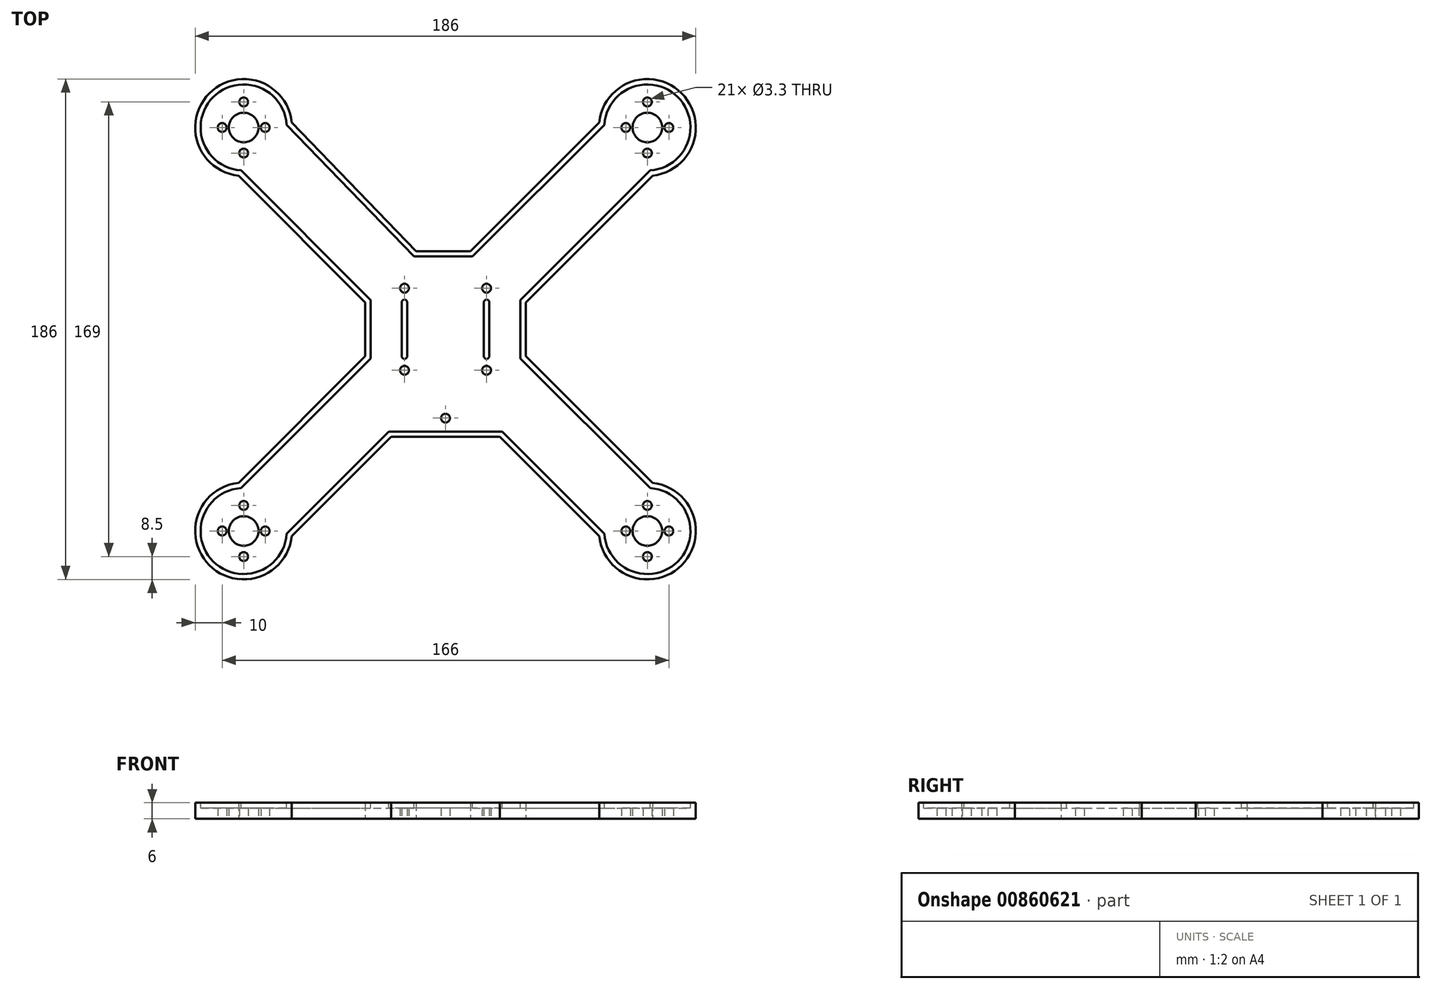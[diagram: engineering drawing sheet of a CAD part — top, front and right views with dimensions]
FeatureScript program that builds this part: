
annotation { "Feature Type Name" : "Feature", "Feature Type Description" : "" }
export const myFeature = defineFeature(function(context is Context, id is Id, definition is map)
    precondition{}
    {
        {
            var Q0;
            Q0=qCreatedBy(makeId("Top.planeOp"),FACE);
            var sketch = newSketch(context, id + "F0", { "sketchPlane" : qUnion([Q0])});
            skLineSegment(sketch, "E0.bottom", {"start": v(75, -75) * mm, "end": v(-75, -75) * mm, "construction": true});
            skLineSegment(sketch, "E0.top", {"start": v(75, 75) * mm, "end": v(-75, 75) * mm, "construction": true});
            skLineSegment(sketch, "E0.left", {"start": v(75, -75) * mm, "end": v(75, 75) * mm, "construction": true});
            skLineSegment(sketch, "E0.right", {"start": v(-75, -75) * mm, "end": v(-75, 75) * mm, "construction": true});
            skPoint(sketch, "E0.middle", {"position": v(0, 0) * mm});
            skLineSegment(sketch, "E1", {"start": v(-75, 75) * mm, "end": v(75, -75) * mm, "construction": true});
            skLineSegment(sketch, "E2", {"start": v(75, 75) * mm, "end": v(-75, -75) * mm, "construction": true});
            skCircle(sketch, "E3", {"center": v(-75, 75) * mm, "radius": 14 * mm, "construction": true});
            skCircle(sketch, "E4", {"center": v(75, 75) * mm, "radius": 14 * mm, "construction": true});
            skCircle(sketch, "E5", {"center": v(-75, -75) * mm, "radius": 14 * mm, "construction": true});
            skCircle(sketch, "E6", {"center": v(75, -75) * mm, "radius": 14 * mm, "construction": true});
            skCircle(sketch, "E7", {"center": v(-75, 75) * mm, "radius": 65 * mm, "construction": true});
            skCircle(sketch, "E8", {"center": v(75, 75) * mm, "radius": 65 * mm, "construction": true});
            skCircle(sketch, "E9", {"center": v(75, -75) * mm, "radius": 65 * mm, "construction": true});
            skCircle(sketch, "E10", {"center": v(-75, -75) * mm, "radius": 65 * mm, "construction": true});
            skPoint(sketch, "E11", {"position": v(29.04, 29.04) * mm});
            skPoint(sketch, "E12", {"position": v(-29.04, 29.04) * mm});
            skPoint(sketch, "E13", {"position": v(-29.04, -29.04) * mm});
            skPoint(sketch, "E14", {"position": v(29.04, -29.04) * mm});
            skLineSegment(sketch, "E15", {"start": v(-65.1, 84.9) * mm, "end": v(84.9, -65.1) * mm, "construction": true});
            skLineSegment(sketch, "E16", {"start": v(-84.9, 65.1) * mm, "end": v(65.1, -84.9) * mm, "construction": true});
            skLineSegment(sketch, "E17", {"start": v(-84.9, -65.1) * mm, "end": v(65.1, 84.9) * mm, "construction": true});
            skLineSegment(sketch, "E18", {"start": v(-65.1, -84.9) * mm, "end": v(84.9, 65.1) * mm, "construction": true});
            skPoint(sketch, "E19", {"position": v(-75, 84.5) * mm});
            skPoint(sketch, "E20", {"position": v(-75, 65.5) * mm});
            skPoint(sketch, "E21", {"position": v(-67, 75) * mm});
            skPoint(sketch, "E22", {"position": v(-83, 75) * mm});
            skPoint(sketch, "E23.MirrorP", {"position": v(75, 84.5) * mm});
            skPoint(sketch, "E24.MirrorP", {"position": v(67, 75) * mm});
            skPoint(sketch, "E25.MirrorP", {"position": v(75, 65.5) * mm});
            skPoint(sketch, "E26.MirrorP", {"position": v(83, 75) * mm});
            skPoint(sketch, "E27.MirrorP", {"position": v(-75, -84.5) * mm});
            skPoint(sketch, "E28.MirrorP", {"position": v(-83, -75) * mm});
            skPoint(sketch, "E29.MirrorP", {"position": v(-75, -65.5) * mm});
            skPoint(sketch, "E30.MirrorP", {"position": v(-67, -75) * mm});
            skPoint(sketch, "E31.MirrorP", {"position": v(67, -75) * mm});
            skPoint(sketch, "E32.MirrorP", {"position": v(75, -84.5) * mm});
            skPoint(sketch, "E33.MirrorP", {"position": v(83, -75) * mm});
            skPoint(sketch, "E34.MirrorP", {"position": v(75, -65.5) * mm});
            skCircle(sketch, "E35", {"center": v(-75, 75) * mm, "radius": 18 * mm, "construction": true});
            skCircle(sketch, "E36", {"center": v(75, 75) * mm, "radius": 18 * mm, "construction": true});
            skCircle(sketch, "E37", {"center": v(-75, -75) * mm, "radius": 18 * mm, "construction": true});
            skCircle(sketch, "E38", {"center": v(75, -75) * mm, "radius": 18 * mm, "construction": true});
            skSolve(sketch);
        }
        {
            var Q0;
            Q0=qCreatedBy(makeId("Top.planeOp"),FACE);
            var sketch = newSketch(context, id + "F1", { "sketchPlane" : qUnion([Q0])});
            skPoint(sketch, "E39.0", {"position": v(-29.04, 29.04) * mm});
            skPoint(sketch, "E40.0", {"position": v(29.04, 29.04) * mm});
            skPoint(sketch, "E41.0", {"position": v(29.04, -29.04) * mm});
            skPoint(sketch, "E42.0", {"position": v(-29.04, -29.04) * mm});
            skLineSegment(sketch, "E43.bottom", {"start": v(29.04, -29.04) * mm, "end": v(-29.04, -29.04) * mm, "construction": true});
            skLineSegment(sketch, "E43.top", {"start": v(29.04, 29.04) * mm, "end": v(-29.04, 29.04) * mm, "construction": true});
            skLineSegment(sketch, "E43.left", {"start": v(29.04, -29.04) * mm, "end": v(29.04, 29.04) * mm, "construction": true});
            skLineSegment(sketch, "E43.right", {"start": v(-29.04, -29.04) * mm, "end": v(-29.04, 29.04) * mm, "construction": true});
            skPoint(sketch, "E43.middle", {"position": v(0, 0) * mm});
            skLineSegment(sketch, "E44.bottom", {"start": v(15.25, -15.25) * mm, "end": v(-15.25, -15.25) * mm, "construction": true});
            skLineSegment(sketch, "E44.top", {"start": v(15.25, 15.25) * mm, "end": v(-15.25, 15.25) * mm, "construction": true});
            skLineSegment(sketch, "E44.left", {"start": v(15.25, -15.25) * mm, "end": v(15.25, -10) * mm, "construction": true});
            skLineSegment(sketch, "E44.right", {"start": v(-15.25, -15.25) * mm, "end": v(-15.25, -10) * mm, "construction": true});
            skLineSegment(sketch, "E45.bottom", {"start": v(25.04, -25.04) * mm, "end": v(-25.04, -25.04) * mm, "construction": true});
            skLineSegment(sketch, "E45.top", {"start": v(25.04, 25.04) * mm, "end": v(-25.04, 25.04) * mm, "construction": true});
            skLineSegment(sketch, "E45.left", {"start": v(25.04, -25.04) * mm, "end": v(25.04, 25.04) * mm, "construction": true});
            skLineSegment(sketch, "E45.right", {"start": v(-25.04, -25.04) * mm, "end": v(-25.04, 25.04) * mm, "construction": true});
            skLineSegment(sketch, "E46", {"start": v(-15.25, 10) * mm, "end": v(-15.25, 15.25) * mm, "construction": true});
            skLineSegment(sketch, "E47", {"start": v(-15.25, -10) * mm, "end": v(-15.25, 10) * mm, "construction": true});
            skLineSegment(sketch, "E48", {"start": v(15.25, 10) * mm, "end": v(15.25, 15.25) * mm, "construction": true});
            skLineSegment(sketch, "E49", {"start": v(15.25, -10) * mm, "end": v(15.25, 10) * mm, "construction": true});
            skPoint(sketch, "E50", {"position": v(0, -29.04) * mm});
            skPoint(sketch, "E51", {"position": v(0, -33.04) * mm});
            skSolve(sketch);
        }
        {
            var Q0;
            Q0=qCreatedBy(makeId("Top.planeOp"),FACE);
            var sketch = newSketch(context, id + "F2", { "sketchPlane" : qUnion([Q0])});
            skCircle(sketch, "E52.0", {"center": v(-75, 75) * mm, "radius": 14 * mm, "construction": true});
            skCircle(sketch, "E53.0", {"center": v(-75, -75) * mm, "radius": 14 * mm, "construction": true});
            skCircle(sketch, "E54.0", {"center": v(75, 75) * mm, "radius": 14 * mm, "construction": true});
            skCircle(sketch, "E55.0", {"center": v(75, -75) * mm, "radius": 14 * mm, "construction": true});
            skLineSegment(sketch, "E56.0", {"start": v(9.24, 29.04) * mm, "end": v(-10.88, 29.04) * mm});
            skLineSegment(sketch, "E57", {"start": v(9.24, 29.04) * mm, "end": v(57.1, 76.9) * mm});
            skLineSegment(sketch, "E58", {"start": v(29.8, -10) * mm, "end": v(29.8, 10) * mm});
            skLineSegment(sketch, "E59", {"start": v(20.22, -40.02) * mm, "end": v(-20.22, -40.02) * mm});
            skLineSegment(sketch, "E60", {"start": v(-29.8, -10) * mm, "end": v(-29.8, 10) * mm});
            skLineSegment(sketch, "E61.trimOffspring", {"start": v(29.8, -10) * mm, "end": v(76.9, -57.1) * mm});
            skLineSegment(sketch, "E62.trimOffspring", {"start": v(20.22, -40.02) * mm, "end": v(57.1, -76.9) * mm});
            skLineSegment(sketch, "E63.trimOffspring", {"start": v(29.8, 10) * mm, "end": v(76.9, 57.1) * mm});
            skPoint(sketch, "E64.end.orphan", {"position": v(-29.04, 29.04) * mm});
            skPoint(sketch, "E65.orphan", {"position": v(29.04, 29.04) * mm});
            skPoint(sketch, "E66.0.start.orphan", {"position": v(29.04, -29.04) * mm});
            skPoint(sketch, "E67.end.orphan", {"position": v(-29.04, -29.04) * mm});
            skLineSegment(sketch, "E68.JG1.JG1", {"start": v(-15.25, -10) * mm, "end": v(-15.25, 10) * mm, "construction": true});
            skLineSegment(sketch, "E68.JG9.JG9", {"start": v(15.25, -10) * mm, "end": v(15.25, 10) * mm, "construction": true});
            skArc(sketch, "E68.0.startCap", {"start": v(-14.25, -10) * mm, "mid": v(-15.25, -11) * mm, "end": v(-16.25, -10) * mm});
            skArc(sketch, "E68.0.endCap", {"start": v(-16.25, 10) * mm, "mid": v(-15.25, 11) * mm, "end": v(-14.25, 10) * mm});
            skLineSegment(sketch, "E68.0.left", {"start": v(-16.25, -10) * mm, "end": v(-16.25, 10) * mm});
            skLineSegment(sketch, "E68.0.right", {"start": v(-14.25, -10) * mm, "end": v(-14.25, 10) * mm});
            skArc(sketch, "E68.1.startCap", {"start": v(16.25, -10) * mm, "mid": v(15.25, -11) * mm, "end": v(14.25, -10) * mm});
            skArc(sketch, "E68.1.endCap", {"start": v(14.25, 10) * mm, "mid": v(15.25, 11) * mm, "end": v(16.25, 10) * mm});
            skLineSegment(sketch, "E68.1.left", {"start": v(14.25, -10) * mm, "end": v(14.25, 10) * mm});
            skLineSegment(sketch, "E68.1.right", {"start": v(16.25, -10) * mm, "end": v(16.25, 10) * mm});
            skArc(sketch, "E69", {"start": v(-57.1, 76.9) * mm, "mid": v(-87.73, 87.73) * mm, "end": v(-76.9, 57.1) * mm});
            skArc(sketch, "E70", {"start": v(57.1, -76.9) * mm, "mid": v(87.73, -87.73) * mm, "end": v(76.9, -57.1) * mm});
            skArc(sketch, "E71", {"start": v(76.9, 57.1) * mm, "mid": v(87.73, 87.73) * mm, "end": v(57.1, 76.9) * mm});
            skLineSegment(sketch, "E72", {"start": v(-76.9, 57.1) * mm, "end": v(-29.8, 10) * mm});
            skLineSegment(sketch, "E73", {"start": v(-57.1, 76.9) * mm, "end": v(-10.88, 29.04) * mm});
            skArc(sketch, "E74", {"start": v(-76.9, -57.1) * mm, "mid": v(-87.73, -87.73) * mm, "end": v(-57.1, -76.9) * mm});
            skLineSegment(sketch, "E75", {"start": v(-76.9, -57.1) * mm, "end": v(-29.8, -10) * mm});
            skLineSegment(sketch, "E76", {"start": v(-57.1, -76.9) * mm, "end": v(-20.22, -40.02) * mm});
            skSolve(sketch);
        }
        {
            var Q0;
            Q0 = qSketchRegion(id + "F2", true);
            extrude(context, id + "F3", {"entities" : qUnion([Q0]), "depth" : 6 * mm, "offsetDistance" : 25 * mm});
        }
        {
            var Q0;
            Q0=makeQuery(id+"F3.opExtrude","CAP_FACE",FACE,{"disambiguationData":[OSD([sQuery(id+"F2.wireOp",EDGE,"E56.0"),sQuery(id+"F2.wireOp",EDGE,"E57"),sQuery(id+"F2.wireOp",EDGE,"E58"),sQuery(id+"F2.wireOp",EDGE,"E59"),sQuery(id+"F2.wireOp",EDGE,"E60"),sQuery(id+"F2.wireOp",EDGE,"E61.trimOffspring"),sQuery(id+"F2.wireOp",EDGE,"E62.trimOffspring"),sQuery(id+"F2.wireOp",EDGE,"E63.trimOffspring"),sQuery(id+"F2.wireOp",EDGE,"E68.0.startCap"),sQuery(id+"F2.wireOp",EDGE,"E68.0.endCap"),sQuery(id+"F2.wireOp",EDGE,"E68.0.left"),sQuery(id+"F2.wireOp",EDGE,"E68.0.right"),sQuery(id+"F2.wireOp",EDGE,"E68.1.startCap"),sQuery(id+"F2.wireOp",EDGE,"E68.1.endCap"),sQuery(id+"F2.wireOp",EDGE,"E68.1.left"),sQuery(id+"F2.wireOp",EDGE,"E68.1.right"),sQuery(id+"F2.wireOp",EDGE,"E69"),sQuery(id+"F2.wireOp",EDGE,"E70"),sQuery(id+"F2.wireOp",EDGE,"E71"),sQuery(id+"F2.wireOp",EDGE,"E72"),sQuery(id+"F2.wireOp",EDGE,"E73"),sQuery(id+"F2.wireOp",EDGE,"E74"),sQuery(id+"F2.wireOp",EDGE,"E75"),sQuery(id+"F2.wireOp",EDGE,"E76")])],"isStart":false});
            var sketch = newSketch(context, id + "F4", { "sketchPlane" : qUnion([Q0])});
            skLineSegment(sketch, "E77.0", {"start": v(-59.03, 76.02) * mm, "end": v(-11.72, 27.04) * mm});
            skLineSegment(sketch, "E77.1", {"start": v(10.07, 27.04) * mm, "end": v(-11.72, 27.04) * mm});
            skLineSegment(sketch, "E77.2", {"start": v(10.07, 27.04) * mm, "end": v(59.03, 76) * mm});
            skArc(sketch, "E77.3", {"start": v(76, 59.03) * mm, "mid": v(86.31, 86.31) * mm, "end": v(59.03, 76) * mm});
            skLineSegment(sketch, "E77.4", {"start": v(27.8, 10.83) * mm, "end": v(76, 59.03) * mm});
            skArc(sketch, "E77.5", {"start": v(-76, -59.03) * mm, "mid": v(-86.31, -86.31) * mm, "end": v(-59.03, -76) * mm});
            skLineSegment(sketch, "E77.6", {"start": v(-76, -59.03) * mm, "end": v(-27.8, -10.83) * mm});
            skLineSegment(sketch, "E77.7", {"start": v(-27.8, -10.83) * mm, "end": v(-27.8, 10.83) * mm});
            skLineSegment(sketch, "E77.8", {"start": v(-76, 59.03) * mm, "end": v(-27.8, 10.83) * mm});
            skLineSegment(sketch, "E77.9", {"start": v(-59.03, -76) * mm, "end": v(-21.05, -38.02) * mm});
            skLineSegment(sketch, "E77.10", {"start": v(21.05, -38.02) * mm, "end": v(-21.05, -38.02) * mm});
            skLineSegment(sketch, "E77.11", {"start": v(21.05, -38.02) * mm, "end": v(59.03, -76) * mm});
            skArc(sketch, "E77.12", {"start": v(59.03, -76) * mm, "mid": v(86.31, -86.31) * mm, "end": v(76, -59.03) * mm});
            skLineSegment(sketch, "E77.13", {"start": v(27.8, -10.83) * mm, "end": v(76, -59.03) * mm});
            skArc(sketch, "E77.14", {"start": v(-59.03, 76.02) * mm, "mid": v(-86.32, 86.3) * mm, "end": v(-76, 59.03) * mm});
            skLineSegment(sketch, "E77.15", {"start": v(27.8, -10.83) * mm, "end": v(27.8, 10.83) * mm});
            skArc(sketch, "E78.0", {"start": v(-57.1, 76.9) * mm, "mid": v(-87.73, 87.73) * mm, "end": v(-76.9, 57.1) * mm});
            skLineSegment(sketch, "E79.0", {"start": v(-57.1, 76.9) * mm, "end": v(-10.88, 29.04) * mm});
            skLineSegment(sketch, "E80.0", {"start": v(9.24, 29.04) * mm, "end": v(57.1, 76.9) * mm});
            skArc(sketch, "E81.0", {"start": v(76.9, 57.1) * mm, "mid": v(87.73, 87.73) * mm, "end": v(57.1, 76.9) * mm});
            skLineSegment(sketch, "E82.0", {"start": v(29.8, 10) * mm, "end": v(76.9, 57.1) * mm});
            skLineSegment(sketch, "E83.0", {"start": v(-76.9, 57.1) * mm, "end": v(-29.8, 10) * mm});
            skLineSegment(sketch, "E84.0", {"start": v(-29.8, -10) * mm, "end": v(-29.8, 10) * mm});
            skLineSegment(sketch, "E85.0", {"start": v(-76.9, -57.1) * mm, "end": v(-29.8, -10) * mm});
            skArc(sketch, "E86.0", {"start": v(-76.9, -57.1) * mm, "mid": v(-87.73, -87.73) * mm, "end": v(-57.1, -76.9) * mm});
            skLineSegment(sketch, "E87.0", {"start": v(-57.1, -76.9) * mm, "end": v(-20.22, -40.02) * mm});
            skLineSegment(sketch, "E88.0", {"start": v(20.22, -40.02) * mm, "end": v(-20.22, -40.02) * mm});
            skLineSegment(sketch, "E89.0", {"start": v(20.22, -40.02) * mm, "end": v(57.1, -76.9) * mm});
            skArc(sketch, "E90.0", {"start": v(57.1, -76.9) * mm, "mid": v(87.73, -87.73) * mm, "end": v(76.9, -57.1) * mm});
            skLineSegment(sketch, "E91.0", {"start": v(29.8, -10) * mm, "end": v(76.9, -57.1) * mm});
            skLineSegment(sketch, "E92.0", {"start": v(29.8, -10) * mm, "end": v(29.8, 10) * mm});
            skSolve(sketch);
        }
        {
            var Q0;
            Q0=sQuery(id+"F0.wireOp",VERTEX,"E22");
            var Q1;
            Q1=sQuery(id+"F0.wireOp",VERTEX,"E19");
            var Q2;
            Q2=sQuery(id+"F0.wireOp",VERTEX,"E21");
            var Q3;
            Q3=sQuery(id+"F0.wireOp",VERTEX,"E20");
            var Q4;
            Q4=sQuery(id+"F0.wireOp",VERTEX,"E29.MirrorP");
            var Q5;
            Q5=sQuery(id+"F0.wireOp",VERTEX,"E28.MirrorP");
            var Q6;
            Q6=sQuery(id+"F0.wireOp",VERTEX,"E27.MirrorP");
            var Q7;
            Q7=sQuery(id+"F0.wireOp",VERTEX,"E30.MirrorP");
            var Q8;
            Q8=sQuery(id+"F0.wireOp",VERTEX,"E31.MirrorP");
            var Q9;
            Q9=sQuery(id+"F0.wireOp",VERTEX,"E34.MirrorP");
            var Q10;
            Q10=sQuery(id+"F0.wireOp",VERTEX,"E33.MirrorP");
            var Q11;
            Q11=sQuery(id+"F0.wireOp",VERTEX,"E32.MirrorP");
            var Q12;
            Q12=sQuery(id+"F0.wireOp",VERTEX,"E25.MirrorP");
            var Q13;
            Q13=sQuery(id+"F0.wireOp",VERTEX,"E24.MirrorP");
            var Q14;
            Q14=sQuery(id+"F0.wireOp",VERTEX,"E23.MirrorP");
            var Q15;
            Q15=sQuery(id+"F0.wireOp",VERTEX,"E26.MirrorP");
            var Q16;
            Q16=sQuery(id+"F1.wireOp",VERTEX,"E44.top.end");
            var Q17;
            Q17=sQuery(id+"F1.wireOp",VERTEX,"E44.top.start");
            var Q18;
            Q18=sQuery(id+"F1.wireOp",VERTEX,"E44.bottom.start");
            var Q19;
            Q19=sQuery(id+"F1.wireOp",VERTEX,"E44.bottom.end");
            var Q20;
            Q20=sQuery(id+"F1.wireOp",VERTEX,"E51");
            var Q21;
            Q21=makeQuery(id+"F3.opExtrude","SWEPT_BODY",BODY,{"disambiguationData":[OSD([sQuery(id+"F2.wireOp",EDGE,"e4138e94-8dce-43d9-a38b-af33a15f5bcd.0"),sQuery(id+"F2.wireOp",EDGE,"E52.0"),sQuery(id+"F2.wireOp",EDGE,"fdf84008-daaf-4d45-9fa4-0ecefda4e088.0"),sQuery(id+"F2.wireOp",EDGE,"6a79c2ff-3965-43cd-a5b3-00df7fb695de.0"),sQuery(id+"F2.wireOp",EDGE,"c10a3564-eb3d-4cc3-bb5d-81a20f883c14.0"),sQuery(id+"F2.wireOp",EDGE,"E53.0"),sQuery(id+"F2.wireOp",EDGE,"E54.0"),sQuery(id+"F2.wireOp",EDGE,"E55.0"),sQuery(id+"F2.wireOp",EDGE,"E56.0"),sQuery(id+"F2.wireOp",EDGE,"E57"),sQuery(id+"F2.wireOp",EDGE,"d5b23aa8-73d1-45b4-b0a5-47cbde7c9a51"),sQuery(id+"F2.wireOp",EDGE,"E58"),sQuery(id+"F2.wireOp",EDGE,"E59"),sQuery(id+"F2.wireOp",EDGE,"E60"),sQuery(id+"F2.wireOp",EDGE,"E61.trimOffspring"),sQuery(id+"F2.wireOp",EDGE,"E62.trimOffspring"),sQuery(id+"F2.wireOp",EDGE,"E63.trimOffspring")])]});
            hole(context, id + "F5", {"style" : HoleStyle.SIMPLE, "endStyle" : HoleEndStyle.THROUGH, "oppositeDirection" : true, "standardTappedOrClearance" : lookupTablePath({ "fit" : "Normal", "standard" : "ISO", "size" : "M3", "type" : "Clearance" }), "standardBlindInLast" : lookupTablePath({ "fit" : "Standard", "standard" : "ISO", "size" : "M3", "type" : "Clearance" }), "holeDiameter" : 3.3 * mm, "majorDiameter" : 5 * mm, "isTappedThrough" : true, "tappedDepth" : 3 * mm, "tapClearance" : 3, "startFromSketch" : true, "locations" : qUnion([Q0, Q1, Q2, Q3, Q4, Q5, Q6, Q7, Q8, Q9, Q10, Q11, Q12, Q13, Q14, Q15, Q16, Q17, Q18, Q19, Q20]), "scope" : qUnion([Q21])});
        }
        {
            var Q0;
            Q0 = qSketchRegion(id + "F4", true);
            extrude(context, id + "F6", {"entities" : qUnion([Q0]), "operationType" : NewBodyOperationType.REMOVE, "oppositeDirection" : true, "depth" : 2 * mm, "offsetDistance" : 25 * mm});
        }
        {
            var Q0;
            Q0=sQuery(id+"F0.wireOp",VERTEX,"E0.top.end");
            var Q1;
            Q1=sQuery(id+"F0.wireOp",VERTEX,"E0.top.start");
            var Q2;
            Q2=sQuery(id+"F0.wireOp",VERTEX,"E0.bottom.end");
            var Q3;
            Q3=sQuery(id+"F0.wireOp",VERTEX,"E0.bottom.start");
            var Q4;
            Q4=makeQuery(id+"F3.opExtrude","SWEPT_BODY",BODY,{"disambiguationData":[OSD([sQuery(id+"F2.wireOp",EDGE,"E56.0"),sQuery(id+"F2.wireOp",EDGE,"E57"),sQuery(id+"F2.wireOp",EDGE,"E58"),sQuery(id+"F2.wireOp",EDGE,"E59"),sQuery(id+"F2.wireOp",EDGE,"E60"),sQuery(id+"F2.wireOp",EDGE,"E61.trimOffspring"),sQuery(id+"F2.wireOp",EDGE,"E62.trimOffspring"),sQuery(id+"F2.wireOp",EDGE,"E63.trimOffspring"),sQuery(id+"F2.wireOp",EDGE,"E68.0.startCap"),sQuery(id+"F2.wireOp",EDGE,"E68.0.endCap"),sQuery(id+"F2.wireOp",EDGE,"E68.0.left"),sQuery(id+"F2.wireOp",EDGE,"E68.0.right"),sQuery(id+"F2.wireOp",EDGE,"E68.1.startCap"),sQuery(id+"F2.wireOp",EDGE,"E68.1.endCap"),sQuery(id+"F2.wireOp",EDGE,"E68.1.left"),sQuery(id+"F2.wireOp",EDGE,"E68.1.right"),sQuery(id+"F2.wireOp",EDGE,"E69"),sQuery(id+"F2.wireOp",EDGE,"E70"),sQuery(id+"F2.wireOp",EDGE,"E71"),sQuery(id+"F2.wireOp",EDGE,"E72"),sQuery(id+"F2.wireOp",EDGE,"E73"),sQuery(id+"F2.wireOp",EDGE,"E74"),sQuery(id+"F2.wireOp",EDGE,"E75"),sQuery(id+"F2.wireOp",EDGE,"E76")])]});
            hole(context, id + "F7", {"style" : HoleStyle.SIMPLE, "endStyle" : HoleEndStyle.THROUGH, "oppositeDirection" : true, "standardTappedOrClearance" : lookupTablePath({ "fit" : "Normal", "standard" : "ISO", "size" : "M10", "type" : "Clearance" }), "standardBlindInLast" : lookupTablePath({ "fit" : "Standard", "standard" : "ISO", "size" : "M10", "type" : "Clearance" }), "holeDiameter" : 11 * mm, "majorDiameter" : 5 * mm, "isTappedThrough" : true, "tappedDepth" : 3 * mm, "tapClearance" : 3, "startFromSketch" : true, "locations" : qUnion([Q0, Q1, Q2, Q3]), "scope" : qUnion([Q4])});
        }
    });
